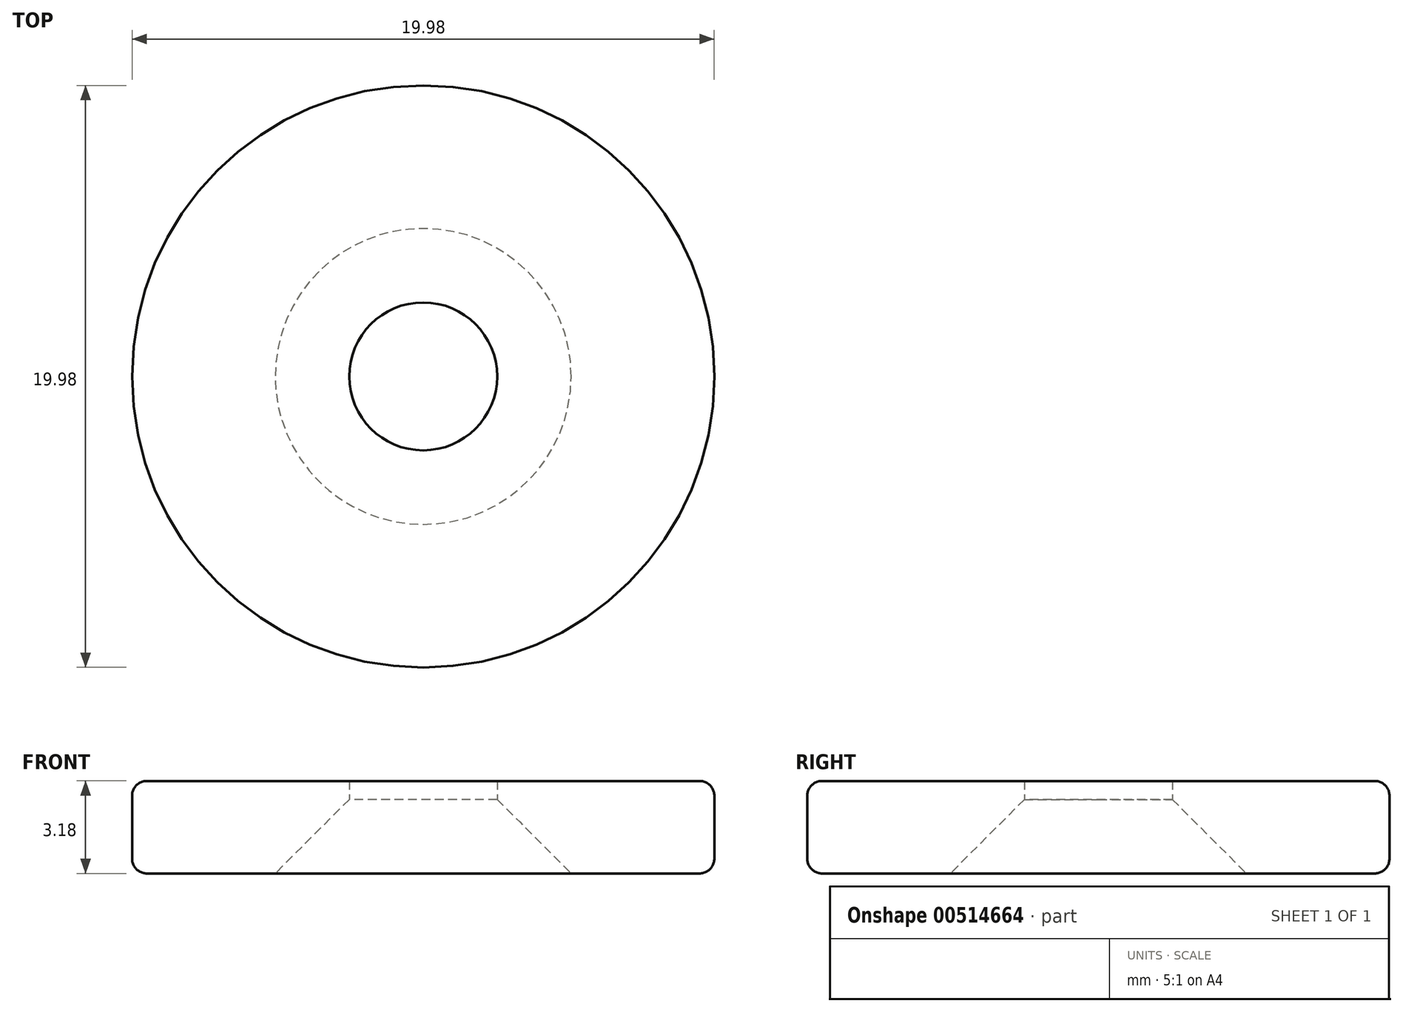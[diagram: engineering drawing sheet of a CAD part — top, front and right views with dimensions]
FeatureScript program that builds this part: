
annotation { "Feature Type Name" : "Feature", "Feature Type Description" : "" }
export const myFeature = defineFeature(function(context is Context, id is Id, definition is map)
    precondition{}
    {
        {
            var Q0;
            Q0=qCreatedBy(makeId("Top.planeOp"),FACE);
            var sketch = newSketch(context, id + "F0", { "sketchPlane" : qUnion([Q0])});
            skCircle(sketch, "E0", {"center": v(0, 0) * mm, "radius": 10 * mm});
            skCircle(sketch, "E1", {"center": v(0, 0) * mm, "radius": 2.54 * mm});
            skSolve(sketch);
        }
        {
            var Q0;
            Q0=makeQuery(id+"F0.imprint","IMPRINT",FACE,{"disambiguationData":[TD([[makeQuery(id+"F0.imprint","IMPRINT",EDGE,{"derivedFrom":sQuery(id+"F0.wireOp",EDGE,"E0")}),1.0]])]});
            extrude(context, id + "F1", {"entities" : qUnion([Q0]), "depth" : 3.17 * mm, "offsetDistance" : 25.4 * mm});
        }
        {
            var Q0;
            Q0=makeQuery(id+"F1.opExtrude","CAP_EDGE",EDGE,{"disambiguationData":[OSD([sQuery(id+"F0.wireOp",EDGE,"E1")])],"isStart":true});
            chamfer(context, id + "F2", {"entities" : qUnion([Q0]), "width" : 2.54 * mm, "tangentPropagation" : true});
        }
        {
            var Q0;
            Q0=makeQuery(id+"F1.opExtrude","CAP_EDGE",EDGE,{"disambiguationData":[OSD([sQuery(id+"F0.wireOp",EDGE,"E0")])],"isStart":false});
            var Q1;
            Q1=makeQuery(id+"F1.opExtrude","CAP_EDGE",EDGE,{"disambiguationData":[OSD([sQuery(id+"F0.wireOp",EDGE,"E0")])],"isStart":true});
            fillet(context, id + "F3", {"entities" : qUnion([Q0, Q1]), "radius" : 0.5 * mm, "tangentPropagation" : true, "allowEdgeOverflow" : false});
        }
    });
